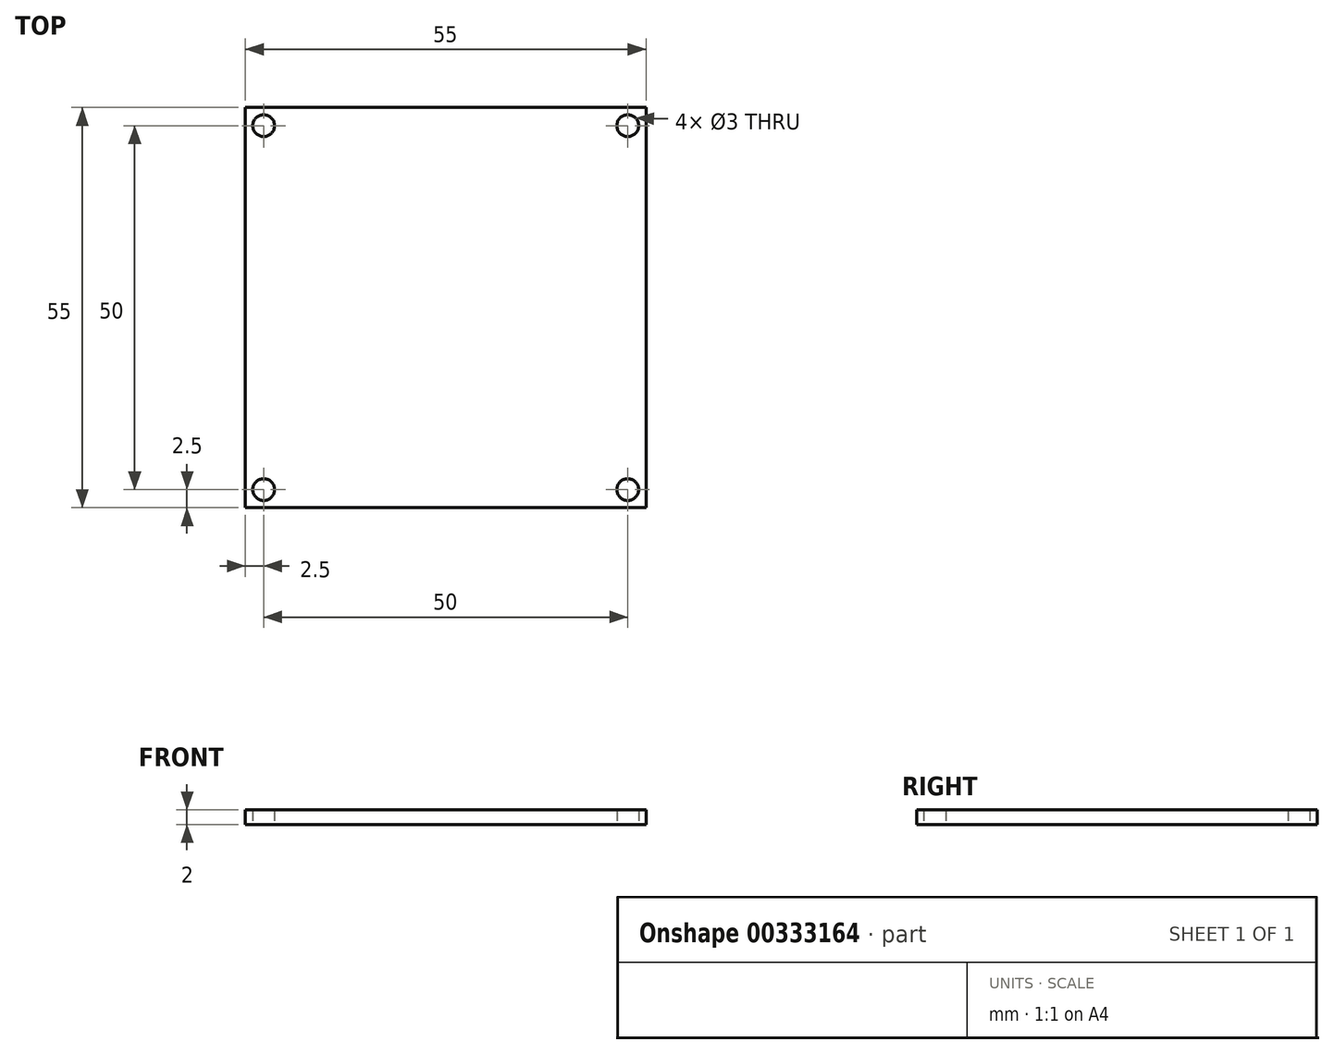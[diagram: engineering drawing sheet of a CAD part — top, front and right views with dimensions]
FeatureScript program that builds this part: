
annotation { "Feature Type Name" : "Feature", "Feature Type Description" : "" }
export const myFeature = defineFeature(function(context is Context, id is Id, definition is map)
    precondition{}
    {
        {
            var Q0;
            Q0=qCreatedBy(makeId("Top.planeOp"),FACE);
            var sketch = newSketch(context, id + "F0", { "sketchPlane" : qUnion([Q0])});
            skLineSegment(sketch, "E0.bottom", {"start": v(27.5, -27.5) * mm, "end": v(-27.5, -27.5) * mm});
            skLineSegment(sketch, "E0.top", {"start": v(27.5, 27.5) * mm, "end": v(-27.5, 27.5) * mm});
            skLineSegment(sketch, "E0.left", {"start": v(27.5, -27.5) * mm, "end": v(27.5, 27.5) * mm});
            skLineSegment(sketch, "E0.right", {"start": v(-27.5, -27.5) * mm, "end": v(-27.5, 27.5) * mm});
            skPoint(sketch, "E0.middle", {"position": v(0, 0) * mm});
            skLineSegment(sketch, "E1.bottom", {"start": v(25, -25) * mm, "end": v(-25, -25) * mm, "construction": true});
            skLineSegment(sketch, "E1.top", {"start": v(25, 25) * mm, "end": v(-25, 25) * mm, "construction": true});
            skLineSegment(sketch, "E1.left", {"start": v(25, -25) * mm, "end": v(25, 25) * mm, "construction": true});
            skLineSegment(sketch, "E1.right", {"start": v(-25, -25) * mm, "end": v(-25, 25) * mm, "construction": true});
            skCircle(sketch, "E2", {"center": v(-25, 25) * mm, "radius": 1.5 * mm});
            skCircle(sketch, "E3.1.0", {"center": v(-25, -25) * mm, "radius": 1.5 * mm});
            skCircle(sketch, "E3.2.0", {"center": v(25, -25) * mm, "radius": 1.5 * mm});
            skCircle(sketch, "E3.3.0", {"center": v(25, 25) * mm, "radius": 1.5 * mm});
            skSolve(sketch);
        }
        {
            var Q0;
            Q0=qSketchRegion(id+"F0",true);
            extrude(context, id + "F1", {"entities" : qUnion([Q0]), "depth" : 2 * mm});
        }
    });
